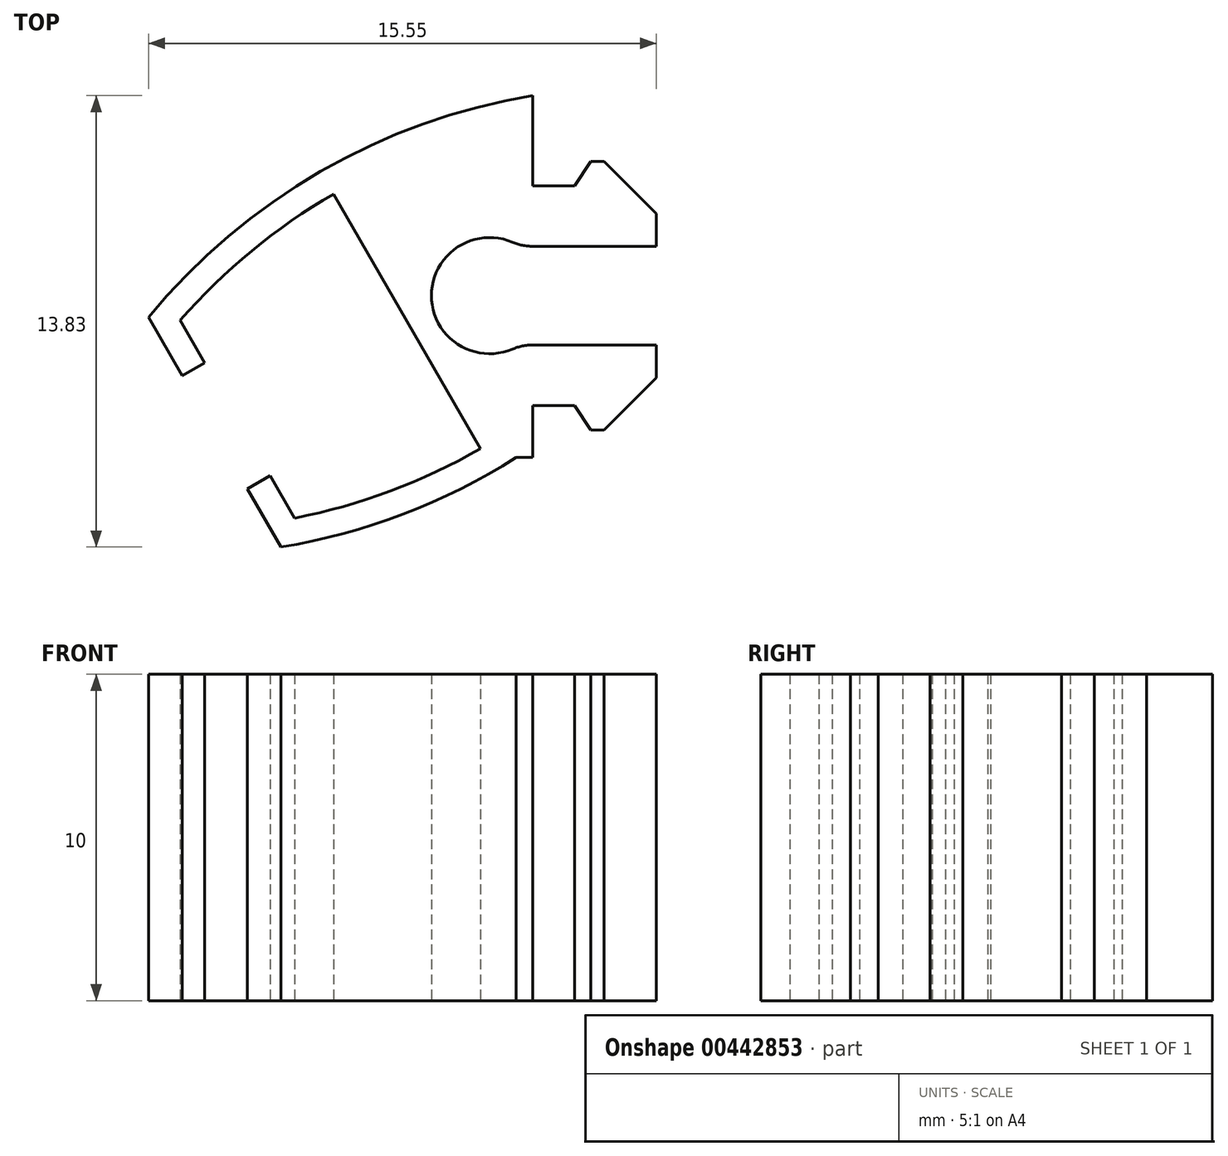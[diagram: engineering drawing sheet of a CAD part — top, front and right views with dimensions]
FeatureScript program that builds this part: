
annotation { "Feature Type Name" : "Feature", "Feature Type Description" : "" }
export const myFeature = defineFeature(function(context is Context, id is Id, definition is map)
    precondition{}
    {
        {
            var Q0;
            Q0=qCreatedBy(makeId("Top.planeOp"),FACE);
            var sketch = newSketch(context, id + "F0", { "sketchPlane" : qUnion([Q0])});
            skLineSegment(sketch, "E0.0", {"start": v(-8.22, -3.11) * mm, "end": v(-10, -3.11) * mm});
            skLineSegment(sketch, "E0.1", {"start": v(-8.22, -7.03) * mm, "end": v(-8.22, -3.11) * mm});
            skLineSegment(sketch, "E0.2", {"start": v(-3.78, -3.11) * mm, "end": v(-8.22, -7.03) * mm});
            skLineSegment(sketch, "E0.3", {"start": v(-3.78, 3.11) * mm, "end": v(-3.78, -3.11) * mm});
            skLineSegment(sketch, "E0.4", {"start": v(-8.22, 7.03) * mm, "end": v(-3.78, 3.11) * mm});
            skLineSegment(sketch, "E0.5", {"start": v(-8.22, 3.11) * mm, "end": v(-8.22, 7.03) * mm});
            skLineSegment(sketch, "E0.6", {"start": v(-10, 3.11) * mm, "end": v(-8.22, 3.11) * mm});
            skLineSegment(sketch, "E0.7", {"start": v(-10, 8.5) * mm, "end": v(-10, 3.11) * mm});
            skArc(sketch, "E0.8", {"start": v(-8.5, 10) * mm, "mid": v(-9.56, 9.56) * mm, "end": v(-10, 8.5) * mm});
            skLineSegment(sketch, "E0.9", {"start": v(-3.11, 10) * mm, "end": v(-8.5, 10) * mm});
            skLineSegment(sketch, "E0.10", {"start": v(-3.11, 8.22) * mm, "end": v(-3.11, 10) * mm});
            skLineSegment(sketch, "E0.11", {"start": v(-10, -3.11) * mm, "end": v(-10, -8.5) * mm});
            skLineSegment(sketch, "E0.12", {"start": v(-7.03, 8.22) * mm, "end": v(-3.11, 8.22) * mm});
            skLineSegment(sketch, "E0.13", {"start": v(-3.11, 3.78) * mm, "end": v(-7.03, 8.22) * mm});
            skLineSegment(sketch, "E0.14", {"start": v(3.11, 3.78) * mm, "end": v(-3.11, 3.78) * mm});
            skLineSegment(sketch, "E0.15", {"start": v(7.03, 8.22) * mm, "end": v(3.11, 3.78) * mm});
            skLineSegment(sketch, "E0.16", {"start": v(3.11, 8.22) * mm, "end": v(7.03, 8.22) * mm});
            skLineSegment(sketch, "E0.17", {"start": v(3.11, 10) * mm, "end": v(3.11, 8.22) * mm});
            skLineSegment(sketch, "E0.18", {"start": v(3.11, -10) * mm, "end": v(8.5, -10) * mm});
            skLineSegment(sketch, "E0.19", {"start": v(3.11, -8.22) * mm, "end": v(3.11, -10) * mm});
            skLineSegment(sketch, "E0.20", {"start": v(7.03, -8.22) * mm, "end": v(3.11, -8.22) * mm});
            skLineSegment(sketch, "E0.21", {"start": v(3.11, -3.78) * mm, "end": v(7.03, -8.22) * mm});
            skLineSegment(sketch, "E0.22", {"start": v(-3.11, -3.78) * mm, "end": v(3.11, -3.78) * mm});
            skLineSegment(sketch, "E0.23", {"start": v(-7.03, -8.22) * mm, "end": v(-3.11, -3.78) * mm});
            skArc(sketch, "E0.24", {"start": v(-10, -8.5) * mm, "mid": v(-9.56, -9.56) * mm, "end": v(-8.5, -10) * mm});
            skLineSegment(sketch, "E0.25", {"start": v(-8.5, -10) * mm, "end": v(-3.11, -10) * mm});
            skLineSegment(sketch, "E0.26", {"start": v(-3.11, -10) * mm, "end": v(-3.11, -8.22) * mm});
            skLineSegment(sketch, "E0.27", {"start": v(-3.11, -8.22) * mm, "end": v(-7.03, -8.22) * mm});
            skArc(sketch, "E0.28", {"start": v(8.5, -10) * mm, "mid": v(9.56, -9.56) * mm, "end": v(10, -8.5) * mm});
            skLineSegment(sketch, "E0.29", {"start": v(10, -8.5) * mm, "end": v(10, -3.11) * mm});
            skLineSegment(sketch, "E0.30", {"start": v(10, -3.11) * mm, "end": v(8.22, -3.11) * mm});
            skLineSegment(sketch, "E0.31", {"start": v(8.22, -3.11) * mm, "end": v(8.22, -7.03) * mm});
            skLineSegment(sketch, "E0.32", {"start": v(8.22, -7.03) * mm, "end": v(3.78, -3.11) * mm});
            skLineSegment(sketch, "E0.33", {"start": v(3.78, -3.11) * mm, "end": v(3.78, 3.11) * mm});
            skLineSegment(sketch, "E0.34", {"start": v(3.78, 3.11) * mm, "end": v(8.22, 7.03) * mm});
            skLineSegment(sketch, "E0.35", {"start": v(8.22, 7.03) * mm, "end": v(8.22, 3.11) * mm});
            skLineSegment(sketch, "E0.36", {"start": v(8.22, 3.11) * mm, "end": v(10, 3.11) * mm});
            skLineSegment(sketch, "E0.37", {"start": v(10, 3.11) * mm, "end": v(10, 8.5) * mm});
            skArc(sketch, "E0.38", {"start": v(10, 8.5) * mm, "mid": v(9.56, 9.56) * mm, "end": v(8.5, 10) * mm});
            skLineSegment(sketch, "E0.39", {"start": v(8.5, 10) * mm, "end": v(3.11, 10) * mm});
            skSolve(sketch);
        }
        {
            var Q0;
            Q0=qCreatedBy(makeId("Top.planeOp"),FACE);
            var sketch = newSketch(context, id + "F1", { "sketchPlane" : qUnion([Q0])});
            skLineSegment(sketch, "E1.right", {"start": v(-16.1, 3.11) * mm, "end": v(-11.6, -4.68) * mm});
            skArc(sketch, "E2", {"start": v(-16.1, 3.11) * mm, "mid": v(-18.6, 1.37) * mm, "end": v(-20.8, -0.75) * mm});
            skLineSegment(sketch, "E3", {"start": v(-13.85, -0.79) * mm, "end": v(-19.05, -3.79) * mm, "construction": true});
            skArc(sketch, "E4.MirrorCS", {"start": v(-11.6, -4.68) * mm, "mid": v(-14.36, -5.99) * mm, "end": v(-17.3, -6.82) * mm});
            skArc(sketch, "E5.0", {"start": v(-15.8, 4.19) * mm, "mid": v(-19.03, 2.06) * mm, "end": v(-21.77, -0.67) * mm});
            skArc(sketch, "E6.0", {"start": v(-10.52, -4.96) * mm, "mid": v(-13.97, -6.7) * mm, "end": v(-17.7, -7.7) * mm});
            skLineSegment(sketch, "E7.0", {"start": v(-21.77, -0.67) * mm, "end": v(-20.74, -2.45) * mm});
            skLineSegment(sketch, "E8", {"start": v(-20.05, -2.05) * mm, "end": v(-20.74, -2.45) * mm});
            skLineSegment(sketch, "E9.MirrorCS", {"start": v(-18.05, -5.52) * mm, "end": v(-18.74, -5.92) * mm});
            skLineSegment(sketch, "E10", {"start": v(-10, 4.19) * mm, "end": v(-10, 3.11) * mm});
            skLineSegment(sketch, "E11", {"start": v(-8.22, 4.11) * mm, "end": v(-7.82, 4.11) * mm});
            skLineSegment(sketch, "E12", {"start": v(-7.82, 4.11) * mm, "end": v(-6.22, 2.51) * mm});
            skLineSegment(sketch, "E13", {"start": v(-6.22, 2.51) * mm, "end": v(-6.22, 1.51) * mm});
            skLineSegment(sketch, "E14", {"start": v(-6.22, 1.51) * mm, "end": v(-10, 1.51) * mm});
            skLineSegment(sketch, "E15", {"start": v(-10, -1.51) * mm, "end": v(-6.22, -1.51) * mm});
            skLineSegment(sketch, "E16", {"start": v(-6.22, -1.51) * mm, "end": v(-6.22, -2.51) * mm});
            skLineSegment(sketch, "E17", {"start": v(-6.22, -2.51) * mm, "end": v(-7.82, -4.11) * mm});
            skLineSegment(sketch, "E18", {"start": v(-7.82, -4.11) * mm, "end": v(-8.22, -4.11) * mm});
            skLineSegment(sketch, "E19", {"start": v(-8.22, -3.11) * mm, "end": v(-10, -3.11) * mm});
            skLineSegment(sketch, "E20", {"start": v(-10, -3.36) * mm, "end": v(-10, -4.96) * mm});
            skLineSegment(sketch, "E21", {"start": v(-10, -4.96) * mm, "end": v(-10.52, -4.96) * mm});
            skArc(sketch, "E22", {"start": v(-10.63, 1.64) * mm, "mid": v(-10.32, 1.54) * mm, "end": v(-10, 1.51) * mm});
            skArc(sketch, "E23", {"start": v(-10, -1.51) * mm, "mid": v(-10.32, -1.54) * mm, "end": v(-10.63, -1.64) * mm});
            skArc(sketch, "E24", {"start": v(-10.63, 1.64) * mm, "mid": v(-13.1, 0) * mm, "end": v(-10.63, -1.64) * mm});
            skPoint(sketch, "E25.orphan", {"position": v(-11.6, 1.51) * mm});
            skPoint(sketch, "E26.orphan", {"position": v(-11.6, -1.51) * mm});
            skLineSegment(sketch, "E27.trimOffspring", {"start": v(-18.05, -5.52) * mm, "end": v(-17.3, -6.82) * mm});
            skLineSegment(sketch, "E28.trimOffspring", {"start": v(-18.74, -5.92) * mm, "end": v(-17.7, -7.7) * mm});
            skLineSegment(sketch, "E29.trimOffspring", {"start": v(-20.8, -0.75) * mm, "end": v(-20.05, -2.05) * mm});
            skPoint(sketch, "E1.bottom.start.orphan", {"position": v(-21.3, 0.11) * mm});
            skPoint(sketch, "E30.trimOffspring.end.orphan", {"position": v(-16.8, -7.68) * mm});
            skLineSegment(sketch, "E31", {"start": v(-10, 3.36) * mm, "end": v(-8.72, 3.36) * mm});
            skLineSegment(sketch, "E32.MirrorCS", {"start": v(-10, -3.36) * mm, "end": v(-8.72, -3.36) * mm});
            skPoint(sketch, "E33.orphan", {"position": v(-8.22, 3.11) * mm});
            skArc(sketch, "E34", {"start": v(-10, 6.13) * mm, "mid": v(-12.98, 5.4) * mm, "end": v(-15.8, 4.19) * mm});
            skLineSegment(sketch, "E35", {"start": v(-10, 6.13) * mm, "end": v(-10, 4.19) * mm});
            skPoint(sketch, "E36.start.orphan", {"position": v(-8.22, 3.36) * mm});
            skPoint(sketch, "E37.orphan", {"position": v(-8.22, -3.36) * mm});
            skLineSegment(sketch, "E38", {"start": v(-8.72, 3.36) * mm, "end": v(-8.22, 4.11) * mm});
            skLineSegment(sketch, "E39", {"start": v(-8.72, -3.36) * mm, "end": v(-8.22, -4.11) * mm});
            skPoint(sketch, "E40.start.orphan", {"position": v(-8.72, -4.11) * mm});
            skSolve(sketch);
        }
        {
            var Q0;
            Q0=makeQuery(id+"F1.imprint","IMPRINT",FACE,{"disambiguationData":[TD([[makeQuery(id+"F1.imprint","IMPRINT",EDGE,{"derivedFrom":sQuery(id+"F1.wireOp",EDGE,"403f437d-ab05-4e4c-a2fd-69a394e8c361.0")}),1.0]])]});
            var Q1;
            {var subQ4=sQuery(id+"F1.wireOp",EDGE,"E1.right");Q1=makeQuery(id+"F1.imprint","IMPRINT",FACE,{"disambiguationData":[TD([[makeQuery(id+"F1.imprint","IMPRINT",EDGE,{"derivedFrom":subQ4}),1.0]])]});}
            var Q2;
            {var subQ0=sQuery(id+"F1.wireOp",EDGE,"E2");Q2=makeQuery(id+"F1.imprint","IMPRINT",FACE,{"disambiguationData":[TD([[makeQuery(id+"F1.imprint","IMPRINT",EDGE,{"derivedFrom":subQ0}),-1.0]])]});}
            var Q3;
            {var subQ3=sQuery(id+"F1.wireOp",EDGE,"E8");Q3=makeQuery(id+"F1.imprint","IMPRINT",FACE,{"disambiguationData":[TD([[makeQuery(id+"F1.imprint","IMPRINT",EDGE,{"derivedFrom":subQ3}),-1.0]])]});}
            var Q4;
            {var subQ6=sQuery(id+"F1.wireOp",EDGE,"E9.MirrorCS");Q4=makeQuery(id+"F1.imprint","IMPRINT",FACE,{"disambiguationData":[TD([[makeQuery(id+"F1.imprint","IMPRINT",EDGE,{"derivedFrom":subQ6}),1.0]])]});}
            var Q5;
            {var subQ0=sQuery(id+"F1.wireOp",EDGE,"E4.MirrorCS");Q5=makeQuery(id+"F1.imprint","IMPRINT",FACE,{"disambiguationData":[TD([[makeQuery(id+"F1.imprint","IMPRINT",EDGE,{"derivedFrom":subQ0}),1.0]])]});}
            extrude(context, id + "F2", {"entities" : qUnion([Q0, Q1, Q2, Q3, Q4, Q5]), "depth" : 10 * mm});
        }
    });
